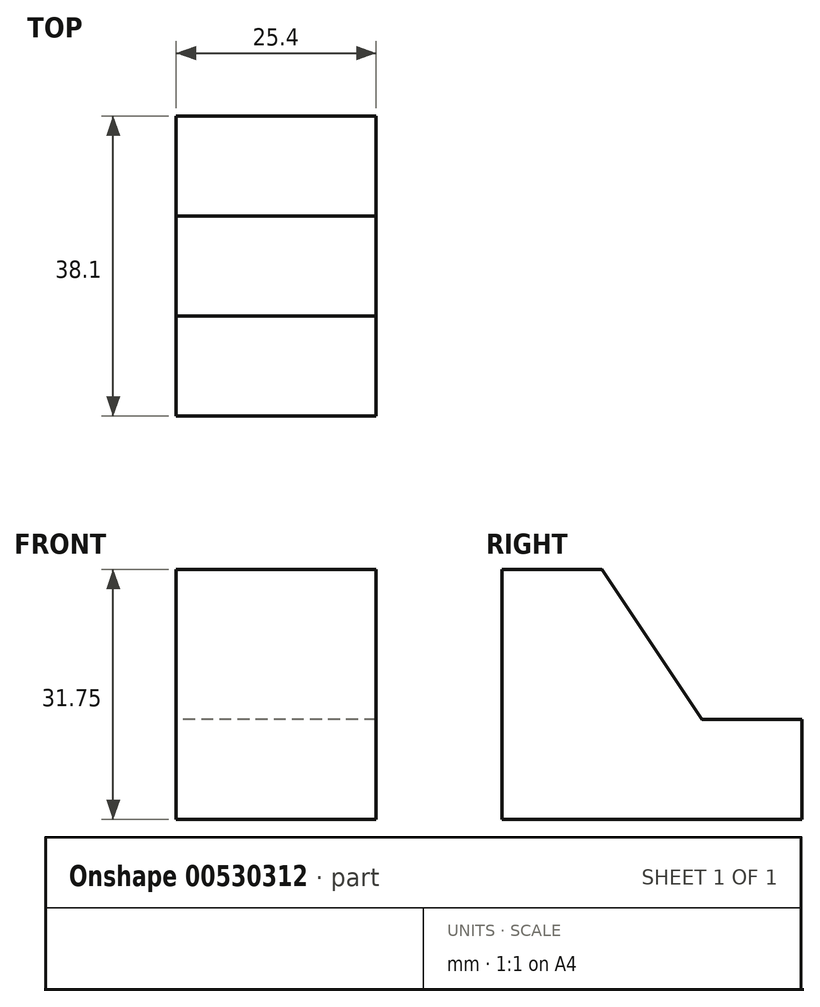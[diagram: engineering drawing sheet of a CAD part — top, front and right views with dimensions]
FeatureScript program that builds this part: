
annotation { "Feature Type Name" : "Feature", "Feature Type Description" : "" }
export const myFeature = defineFeature(function(context is Context, id is Id, definition is map)
    precondition{}
    {
        {
            var Q0;
            Q0=qCreatedBy(makeId("Right.planeOp"),FACE);
            var sketch = newSketch(context, id + "F0", { "sketchPlane" : qUnion([Q0])});
            skLineSegment(sketch, "E0", {"start": v(-15.87, 0) * mm, "end": v(-53.97, 0) * mm});
            skLineSegment(sketch, "E1", {"start": v(-53.97, 0) * mm, "end": v(-53.97, 31.75) * mm});
            skLineSegment(sketch, "E2", {"start": v(-53.97, 31.75) * mm, "end": v(-41.27, 31.75) * mm});
            skLineSegment(sketch, "E3", {"start": v(-15.87, 0) * mm, "end": v(-15.87, 12.7) * mm});
            skLineSegment(sketch, "E4", {"start": v(-15.87, 12.7) * mm, "end": v(-28.57, 12.7) * mm});
            skLineSegment(sketch, "E5", {"start": v(-28.57, 12.7) * mm, "end": v(-41.27, 31.75) * mm});
            skSolve(sketch);
        }
        {
            var Q0;
            Q0=makeQuery(id+"F0.imprint","IMPRINT",FACE,{"disambiguationData":[TD([[makeQuery(id+"F0.imprint","IMPRINT",EDGE,{"derivedFrom":sQuery(id+"F0.wireOp",EDGE,"E0")}),-1.0]])]});
            extrude(context, id + "F1", {"entities" : qUnion([Q0]), "depth" : 25.4 * mm, "offsetDistance" : 25.4 * mm});
        }
    });
